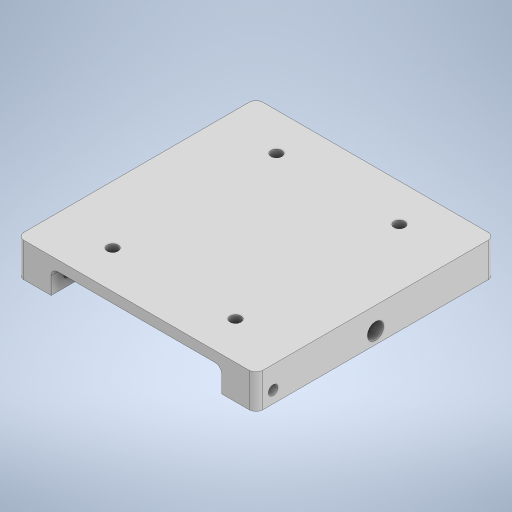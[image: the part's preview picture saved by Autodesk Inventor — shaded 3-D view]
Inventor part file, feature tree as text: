
AUTODESK INVENTOR PART (.ipt)
format: ipt  version: 2024 (Build 280153000, 153)  size: 249,856 bytes
history: native  units: mm
features: sketch x5, hole x3, extrude x2, other x1, fillet x1
ambient origin geometry x8: Origin, YZ Plane, XZ Plane, XY Plane, X Axis, Y Axis, Z Axis, Center Point
bodies: Body1 (feature_tree)
feature tree (12):
  other  "ソリッド1"
  extrude  "押し出し1"  Depth=70.0mm
  extrude  "押し出し2"  Depth=70.0mm
  hole  "穴1"  [1 undecoded]
  hole  "穴2"  [1 undecoded]
  hole  "穴3"  [1 undecoded]
  fillet  "フィレット1"  Radius=3.5mm
  sketch  "スケッチ1"
  sketch  "スケッチ2"
  sketch  "スケッチ3"
  sketch  "スケッチ4"
  sketch  "スケッチ5"
note: 3 required parameter values undecoded (feature->parameter linkage not recoverable at this tier; creation-order binding heuristic only, values carry confidence <= 0.55)
